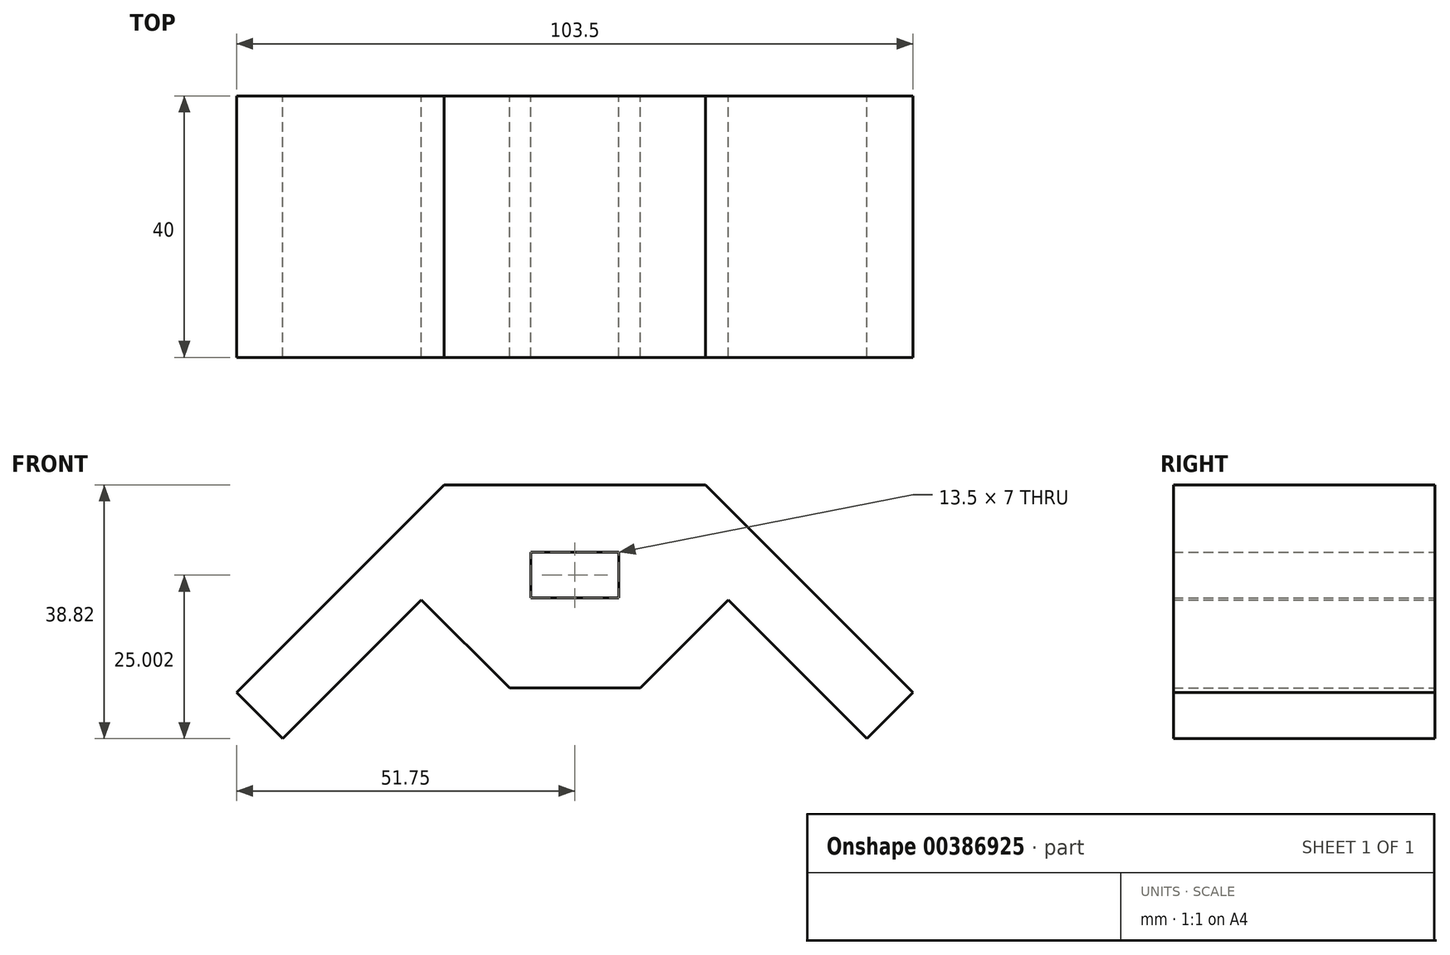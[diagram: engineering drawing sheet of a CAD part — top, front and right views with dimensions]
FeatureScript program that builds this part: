
annotation { "Feature Type Name" : "Feature", "Feature Type Description" : "" }
export const myFeature = defineFeature(function(context is Context, id is Id, definition is map)
    precondition{}
    {
        {
            var Q0;
            Q0=qCreatedBy(makeId("Front.planeOp"),FACE);
            var sketch = newSketch(context, id + "F0", { "sketchPlane" : qUnion([Q0])});
            skLineSegment(sketch, "E0", {"start": v(0, 0) * mm, "end": v(0, 43.07) * mm, "construction": true});
            skLineSegment(sketch, "E1", {"start": v(0, 0) * mm, "end": v(-10, 0) * mm});
            skLineSegment(sketch, "E2", {"start": v(-10, 0) * mm, "end": v(-23.47, 13.47) * mm});
            skLineSegment(sketch, "E3", {"start": v(-23.47, 13.47) * mm, "end": v(-44.68, -7.74) * mm});
            skLineSegment(sketch, "E4", {"start": v(-44.68, -7.74) * mm, "end": v(-51.75, -0.67) * mm});
            skLineSegment(sketch, "E5", {"start": v(-51.75, -0.67) * mm, "end": v(-20, 31.08) * mm});
            skLineSegment(sketch, "E6", {"start": v(-20, 31.08) * mm, "end": v(0, 31.08) * mm});
            skLineSegment(sketch, "E7.MirrorCS", {"start": v(0, 0) * mm, "end": v(10, 0) * mm});
            skLineSegment(sketch, "E8.MirrorCS", {"start": v(20, 31.08) * mm, "end": v(0, 31.08) * mm});
            skLineSegment(sketch, "E9.MirrorCS", {"start": v(51.75, -0.67) * mm, "end": v(20, 31.08) * mm});
            skLineSegment(sketch, "E10.MirrorCS", {"start": v(23.47, 13.47) * mm, "end": v(44.68, -7.74) * mm});
            skLineSegment(sketch, "E11.MirrorCS", {"start": v(10, 0) * mm, "end": v(23.47, 13.47) * mm});
            skLineSegment(sketch, "E12.MirrorCS", {"start": v(44.68, -7.74) * mm, "end": v(51.75, -0.67) * mm});
            skLineSegment(sketch, "E13.bottom", {"start": v(6.75, 20.76) * mm, "end": v(-6.75, 20.76) * mm});
            skLineSegment(sketch, "E13.top", {"start": v(6.75, 13.76) * mm, "end": v(-6.75, 13.76) * mm});
            skLineSegment(sketch, "E13.left", {"start": v(6.75, 20.76) * mm, "end": v(6.75, 13.76) * mm});
            skLineSegment(sketch, "E13.right", {"start": v(-6.75, 20.76) * mm, "end": v(-6.75, 13.76) * mm});
            skPoint(sketch, "E13.middle", {"position": v(0, 17.26) * mm});
            skSolve(sketch);
        }
        {
            var Q0;
            Q0=makeQuery(id+"F0.imprint","IMPRINT",FACE,{"disambiguationData":[TD([[makeQuery(id+"F0.imprint","IMPRINT",EDGE,{"derivedFrom":sQuery(id+"F0.wireOp",EDGE,"E1")}),-1.0]])]});
            extrude(context, id + "F1", {"entities" : qUnion([Q0]), "depth" : 40 * mm});
        }
    });
